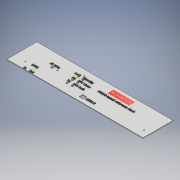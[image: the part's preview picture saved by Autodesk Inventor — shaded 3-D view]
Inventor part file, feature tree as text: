
AUTODESK INVENTOR PART (.ipt)
format: ipt  version: 2018.2 (Build 222227000, 227)  size: 2,074,624 bytes
history: native  units: mm
features: other x3, extrude x2
ambient origin geometry x8: Origin, YZ Plane, XZ Plane, XY Plane, X Axis, Y Axis, Z Axis, Center Point
bodies: Body1 (feature_tree)
feature tree (5):
  other  "Cutouts"
  extrude  "EmbossedText"  Depth=88.0mm
  extrude  "2mm_panel"  Depth=12.0mm
  other  "Text"
  other  "Logo"
